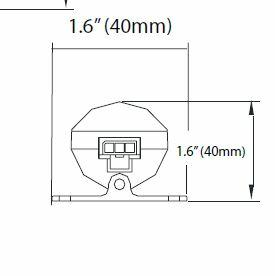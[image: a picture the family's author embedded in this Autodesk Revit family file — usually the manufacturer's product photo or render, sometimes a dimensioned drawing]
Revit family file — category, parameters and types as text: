
# Revit family: Lighting-Surface-Acclaim-Flex 120
name_source: partatom
category: Lighting Fixtures
revit_build: Autodesk Revit 2016 (Build: 20170117_1200(x64)
units: mm (PartAtom-declared; Revit-internal decimal feet)

## family parameters
Cut with Voids When Loaded = No
Host = Face
Light Source = Yes
Part Type = Normal
Room Calculation Point = No
Round Connector Dimension = Use Diameter
Shared = No

## types (1)
- Lighting-Surface-Acclaim-Flex 120
    Apparent Load = 0 VA
    Color Filter = 16777215
    Default Elevation = 48 "
    Description = Linear LED Strip
    Dimming Lamp Color Temperature Shift = <None>
    Emit from Line Length = 24 "
    Height = 0.48 "
    Housing Finish = Aluminum
    Lamp = LED
    Length = 24 "
    Manufacturer = Acclaim Lighting
    Model = Flex 120
    Number of Poles = 1
    Photometric Web File = Load File
    Power Factor = 1
    Tilt Angle = 90.00°
    URL = http://www.acclaimlighting.com
    Voltage = 0 V
    Width = 0.75 "

## geometry (parser evidence)
native form markers: Blend x13, Sweep x3
no freeform markers — native parametric forms only
